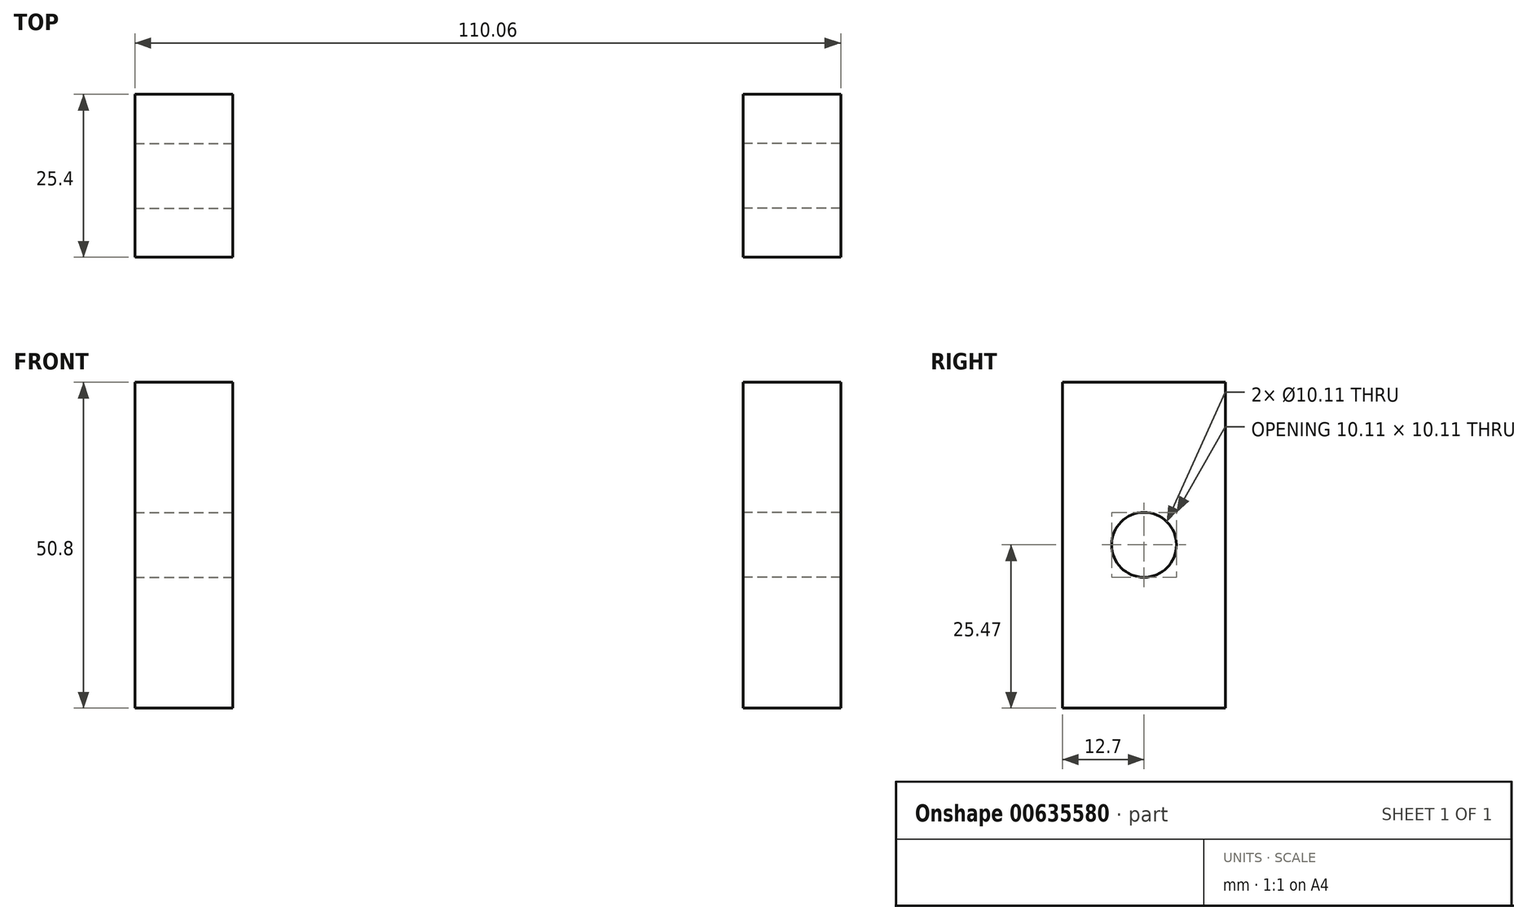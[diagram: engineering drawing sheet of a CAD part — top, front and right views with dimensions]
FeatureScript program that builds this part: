
annotation { "Feature Type Name" : "Feature", "Feature Type Description" : "" }
export const myFeature = defineFeature(function(context is Context, id is Id, definition is map)
    precondition{}
    {
        {
            var Q0;
            Q0=qCreatedBy(makeId("Front.planeOp"),FACE);
            var sketch = newSketch(context, id + "F0", { "sketchPlane" : qUnion([Q0])});
            skLineSegment(sketch, "E0.bottom", {"start": v(-55.03, -19.21) * mm, "end": v(-39.8, -19.21) * mm});
            skLineSegment(sketch, "E0.top", {"start": v(-55.03, 31.59) * mm, "end": v(-39.8, 31.59) * mm});
            skLineSegment(sketch, "E0.left", {"start": v(-55.03, -19.21) * mm, "end": v(-55.03, 31.59) * mm});
            skLineSegment(sketch, "E0.right", {"start": v(-39.8, -19.21) * mm, "end": v(-39.8, 31.59) * mm});
            skSolve(sketch);
        }
        {
            var Q0;
            Q0 = qSketchRegion(id + "F0", true);
            extrude(context, id + "F1", {"entities" : qUnion([Q0]), "depth" : 25.4 * mm, "offsetDistance" : 25.4 * mm});
        }
        {
            var Q0;
            Q0=makeQuery(id+"F1.opExtrude","SWEPT_FACE",FACE,{"disambiguationData":[OSD([sQuery(id+"F0.wireOp",EDGE,"E0.right")])]});
            var sketch = newSketch(context, id + "F2", { "sketchPlane" : qUnion([Q0])});
            skCircle(sketch, "E1", {"center": v(-12.7, 6.26) * mm, "radius": 5.06 * mm});
            skSolve(sketch);
        }
        {
            var Q0;
            Q0=makeQuery(id+"F2.imprint","IMPRINT",FACE,{"disambiguationData":[TD([[makeQuery(id+"F2.imprint","IMPRINT",EDGE,{"derivedFrom":sQuery(id+"F2.wireOp",EDGE,"E1")}),1.0]])]});
            extrude(context, id + "F3", {"entities" : qUnion([Q0]), "operationType" : NewBodyOperationType.REMOVE, "oppositeDirection" : true, "depth" : 25.4 * mm, "offsetDistance" : 25.4 * mm});
        }
        {
            var Q0;
            Q0=makeQuery(id+"F1.opExtrude","SWEPT_BODY",BODY,{"disambiguationData":[OSD([sQuery(id+"F0.wireOp",EDGE,"E0.bottom"),sQuery(id+"F0.wireOp",EDGE,"E0.top"),sQuery(id+"F0.wireOp",EDGE,"E0.left"),sQuery(id+"F0.wireOp",EDGE,"E0.right")])]});
            var Q1;
            Q1=qCreatedBy(makeId("Right.planeOp"),FACE);
            mirror(context, id + "F4", {"entities" : qUnion([Q0]), "mirrorPlane" : qUnion([Q1])});
        }
    });
